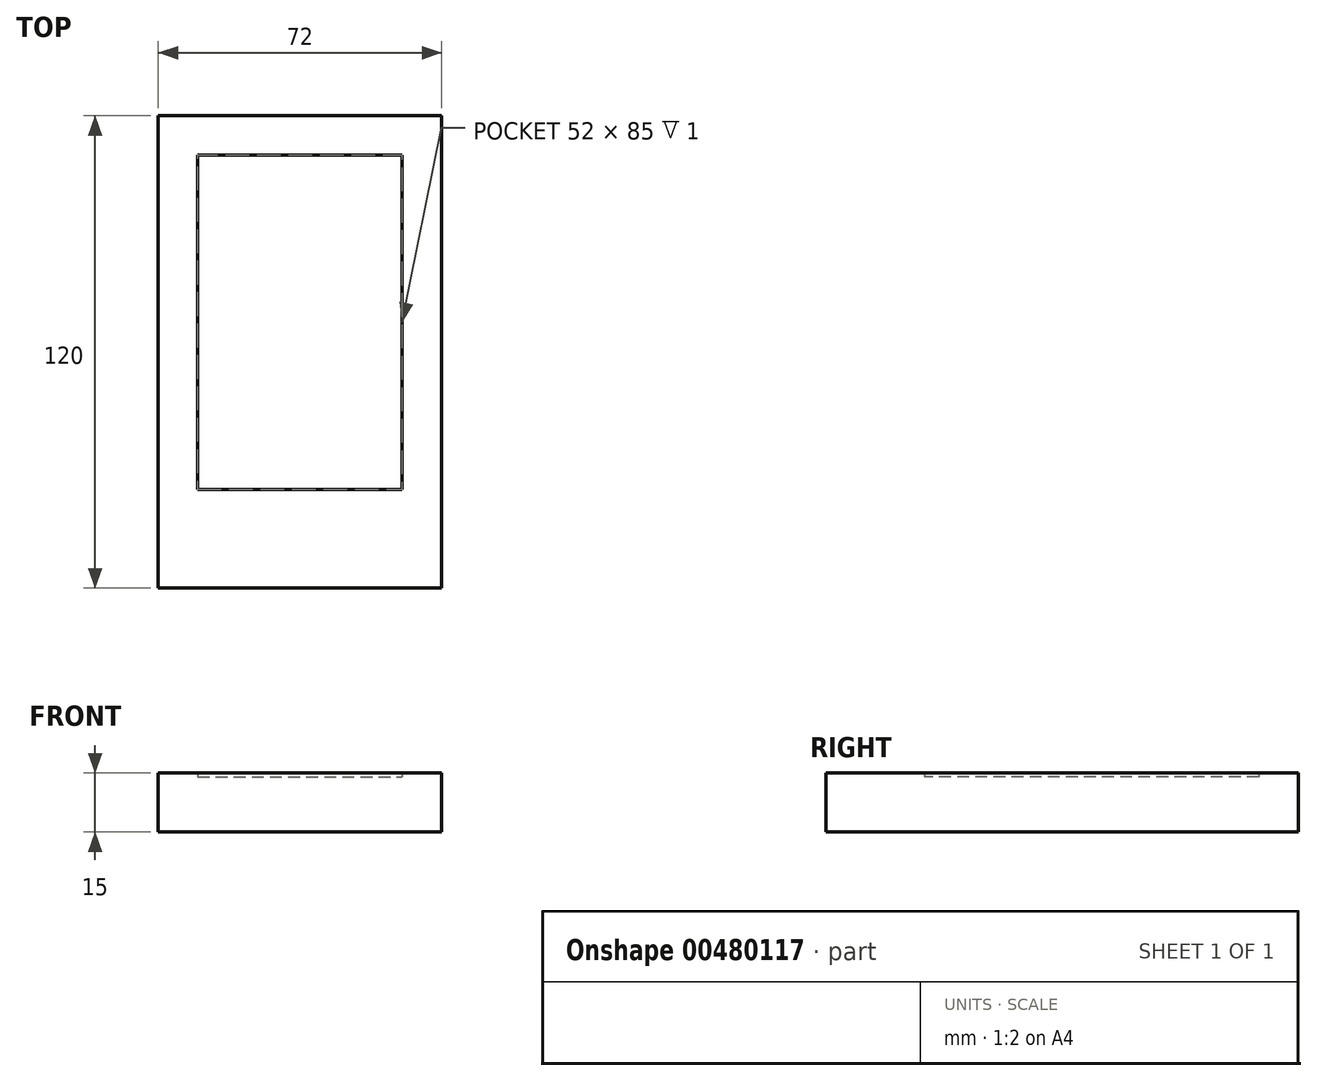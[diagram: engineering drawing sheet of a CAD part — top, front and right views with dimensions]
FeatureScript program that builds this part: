
annotation { "Feature Type Name" : "Feature", "Feature Type Description" : "" }
export const myFeature = defineFeature(function(context is Context, id is Id, definition is map)
    precondition{}
    {
        {
            var Q0;
            Q0=qCreatedBy(makeId("Top.planeOp"),FACE);
            var sketch = newSketch(context, id + "F0", { "sketchPlane" : qUnion([Q0])});
            skLineSegment(sketch, "E0.bottom", {"start": v(36, 60) * mm, "end": v(-36, 60) * mm});
            skLineSegment(sketch, "E0.top", {"start": v(36, -60) * mm, "end": v(-36, -60) * mm});
            skLineSegment(sketch, "E0.left", {"start": v(36, 60) * mm, "end": v(36, -60) * mm});
            skLineSegment(sketch, "E0.right", {"start": v(-36, 60) * mm, "end": v(-36, -60) * mm});
            skPoint(sketch, "E0.middle", {"position": v(0, 0) * mm});
            skLineSegment(sketch, "E1", {"start": v(-26, -35) * mm, "end": v(26, -35) * mm});
            skLineSegment(sketch, "E2", {"start": v(-26, 50) * mm, "end": v(26, 50) * mm});
            skLineSegment(sketch, "E3", {"start": v(-26, 50) * mm, "end": v(-26, -35) * mm});
            skLineSegment(sketch, "E4", {"start": v(26, 50) * mm, "end": v(26, -35) * mm});
            skSolve(sketch);
        }
        {
            var Q0;
            Q0 = qSketchRegion(id + "F0", true);
            var Q1;
            Q1=makeQuery(id+"F0.imprint","IMPRINT",FACE,{"disambiguationData":[TD([[makeQuery(id+"F0.imprint","IMPRINT",EDGE,{"derivedFrom":sQuery(id+"F0.wireOp",EDGE,"E0.bottom")}),1.0]])]});
            extrude(context, id + "F1", {"entities" : qUnion([Q0, Q1]), "depth" : 15 * mm});
        }
        {
            var Q0;
            Q0=makeQuery(id+"F0.imprint","IMPRINT",FACE,{"disambiguationData":[TD([[makeQuery(id+"F0.imprint","IMPRINT",EDGE,{"derivedFrom":sQuery(id+"F0.wireOp",EDGE,"E1")}),1.0]])]});
            extrude(context, id + "F2", {"entities" : qUnion([Q0]), "operationType" : NewBodyOperationType.ADD, "depth" : 14 * mm});
        }
    });
